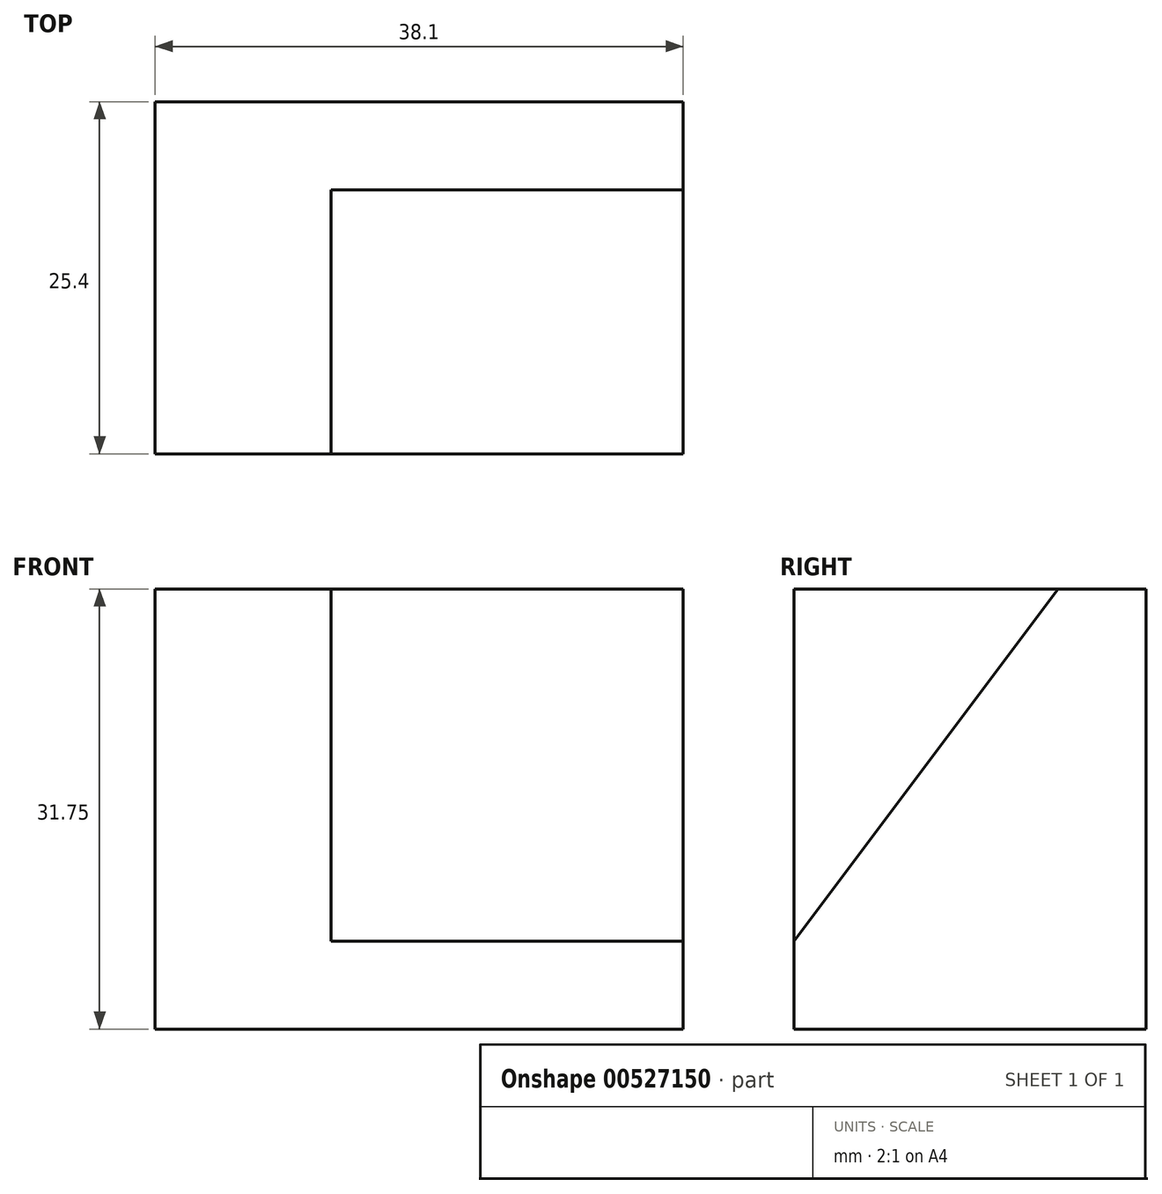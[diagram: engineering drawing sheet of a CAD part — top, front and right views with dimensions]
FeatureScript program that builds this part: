
annotation { "Feature Type Name" : "Feature", "Feature Type Description" : "" }
export const myFeature = defineFeature(function(context is Context, id is Id, definition is map)
    precondition{}
    {
        {
            var Q0;
            Q0=qCreatedBy(makeId("Front.planeOp"),FACE);
            var sketch = newSketch(context, id + "F0", { "sketchPlane" : qUnion([Q0])});
            skLineSegment(sketch, "E0", {"start": v(-48.99, 31.75) * mm, "end": v(-48.99, 0) * mm});
            skLineSegment(sketch, "E1", {"start": v(-48.99, 0) * mm, "end": v(-10.89, 0) * mm});
            skLineSegment(sketch, "E2", {"start": v(-10.89, 0) * mm, "end": v(-10.89, 31.75) * mm});
            skLineSegment(sketch, "E3", {"start": v(-10.89, 31.75) * mm, "end": v(-48.99, 31.75) * mm});
            skSolve(sketch);
        }
        {
            var Q0;
            Q0=makeQuery(id+"F0.imprint","IMPRINT",FACE,{"disambiguationData":[TD([[makeQuery(id+"F0.imprint","IMPRINT",EDGE,{"derivedFrom":sQuery(id+"F0.wireOp",EDGE,"E0")}),1.0]])]});
            extrude(context, id + "F1", {"entities" : qUnion([Q0]), "depth" : 25.4 * mm, "offsetDistance" : 25.4 * mm});
        }
        {
            var Q0;
            Q0=makeQuery(id+"F1.opExtrude","SWEPT_FACE",FACE,{"disambiguationData":[OSD([sQuery(id+"F0.wireOp",EDGE,"E2")])]});
            var sketch = newSketch(context, id + "F2", { "sketchPlane" : qUnion([Q0])});
            skLineSegment(sketch, "E4", {"start": v(-6.35, 31.75) * mm, "end": v(-25.4, 6.35) * mm});
            skSolve(sketch);
        }
        {
            var Q0;
            {var subQ0=sQuery(id+"F2.wireOp",EDGE,"E4");Q0=makeQuery(id+"F2.imprint","IMPRINT",FACE,{"disambiguationData":[TD([[makeQuery(id+"F2.imprint","IMPRINT",EDGE,{"derivedFrom":subQ0}),-1.0]])]});}
            extrude(context, id + "F3", {"entities" : qUnion([Q0]), "operationType" : NewBodyOperationType.REMOVE, "oppositeDirection" : true, "depth" : 25.4 * mm, "offsetDistance" : 25.4 * mm});
        }
    });
